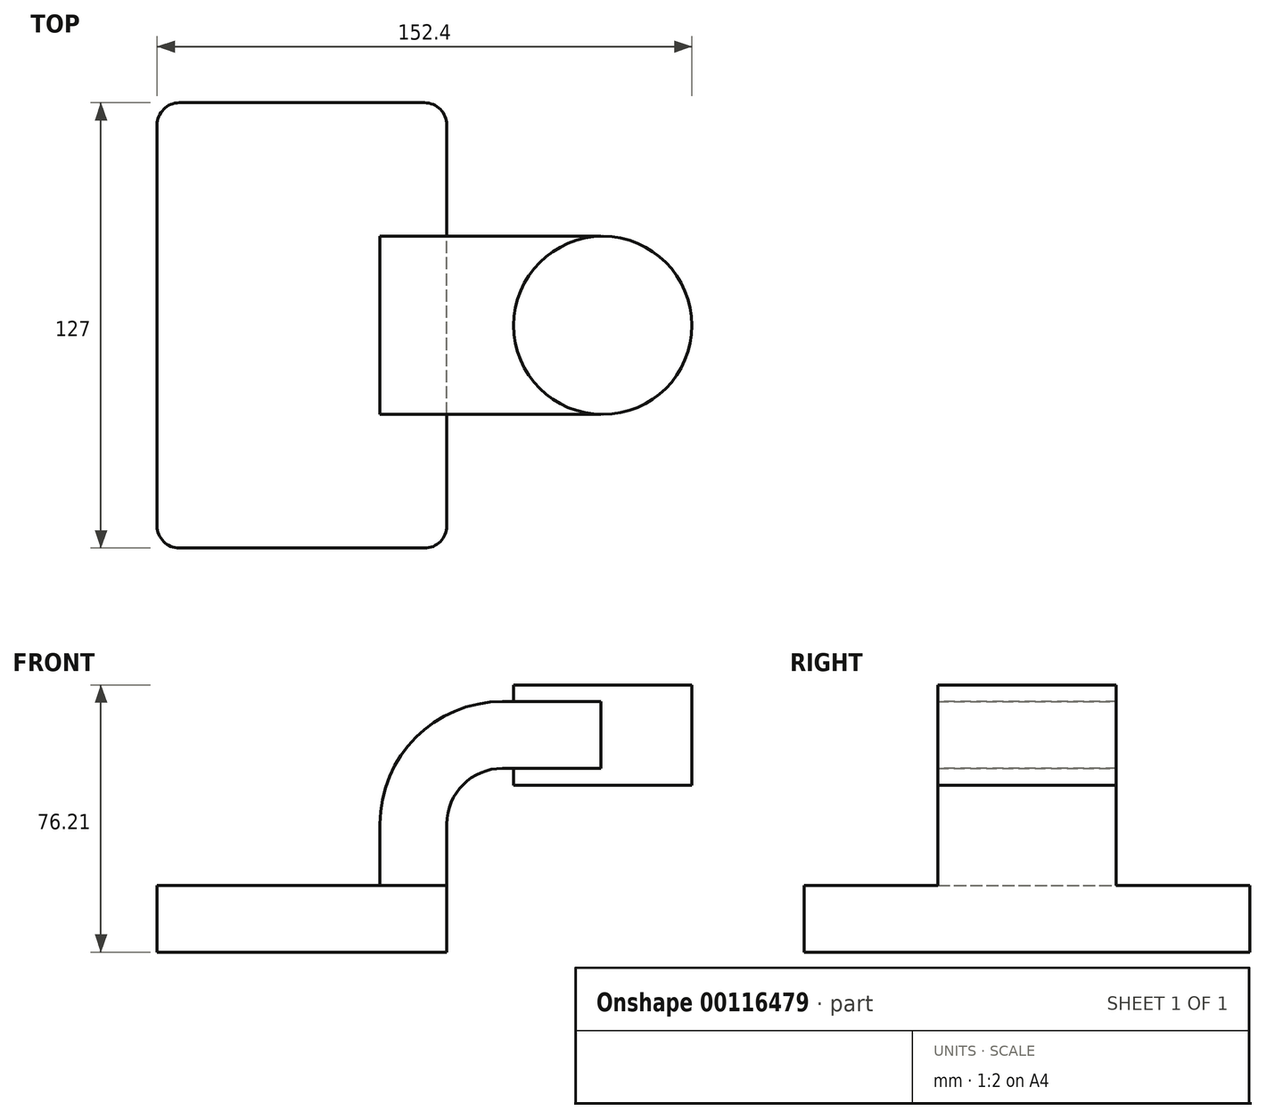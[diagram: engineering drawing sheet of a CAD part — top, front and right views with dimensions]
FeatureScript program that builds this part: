
annotation { "Feature Type Name" : "Feature", "Feature Type Description" : "" }
export const myFeature = defineFeature(function(context is Context, id is Id, definition is map)
    precondition{}
    {
        {
            var Q0;
            Q0=qCreatedBy(makeId("Front.planeOp"),FACE);
            var sketch = newSketch(context, id + "F0", { "sketchPlane" : qUnion([Q0])});
            skLineSegment(sketch, "E0.bottom", {"start": v(41.28, -9.52) * mm, "end": v(-41.28, -9.53) * mm});
            skLineSegment(sketch, "E0.top", {"start": v(41.27, 9.53) * mm, "end": v(-41.28, 9.53) * mm});
            skLineSegment(sketch, "E0.left", {"start": v(41.28, -9.52) * mm, "end": v(41.28, 9.53) * mm});
            skLineSegment(sketch, "E0.right", {"start": v(-41.28, -9.52) * mm, "end": v(-41.28, 9.53) * mm});
            skPoint(sketch, "E0.middle", {"position": v(0, 0) * mm});
            skLineSegment(sketch, "E1.bottom", {"start": v(60.32, 38.1) * mm, "end": v(111.12, 38.1) * mm});
            skLineSegment(sketch, "E1.top", {"start": v(60.32, 66.68) * mm, "end": v(111.12, 66.68) * mm});
            skLineSegment(sketch, "E1.left", {"start": v(60.32, 38.1) * mm, "end": v(60.32, 66.68) * mm});
            skLineSegment(sketch, "E1.right", {"start": v(111.12, 38.1) * mm, "end": v(111.12, 66.68) * mm});
            skPoint(sketch, "E1.middle", {"position": v(85.72, 52.39) * mm});
            skLineSegment(sketch, "E2", {"start": v(41.27, 9.53) * mm, "end": v(41.27, 27) * mm});
            skArc(sketch, "E3", {"start": v(41.27, 27) * mm, "mid": v(45.92, 38.23) * mm, "end": v(57.15, 42.88) * mm});
            skLineSegment(sketch, "E4", {"start": v(57.15, 42.88) * mm, "end": v(85.72, 42.88) * mm});
            skLineSegment(sketch, "E5.0", {"start": v(57.15, 61.93) * mm, "end": v(85.72, 61.93) * mm});
            skArc(sketch, "E5.1", {"start": v(22.23, 27) * mm, "mid": v(32.45, 51.7) * mm, "end": v(57.15, 61.93) * mm});
            skLineSegment(sketch, "E5.2", {"start": v(22.22, 9.53) * mm, "end": v(22.22, 27) * mm});
            skLineSegment(sketch, "E6", {"start": v(85.72, 66.68) * mm, "end": v(85.72, 38.1) * mm});
            skPoint(sketch, "E6.startSnap0", {"position": v(85.72, 66.68) * mm});
            skFitSpline(sketch, "E7", {"points": [v(-41.28, 9.53) * mm, v(57.15, 61.93) * mm], "startDerivative": vector(123.83, 60.16) * mm, "endDerivative": vector(171.45, -18.85) * mm});
            skSolve(sketch);
        }
        {
            var Q0;
            Q0=makeQuery(id+"F0.imprint","IMPRINT",FACE,{"disambiguationData":[TD([[makeQuery(id+"F0.imprint","IMPRINT",EDGE,{"derivedFrom":sQuery(id+"F0.wireOp",EDGE,"E0.bottom")}),-1.0]])]});
            extrude(context, id + "F1", {"entities" : qUnion([Q0]), "endBound" : BoundingType.SYMMETRIC, "depth" : 127 * mm});
        }
        {
            var Q0;
            {var subQ1=sQuery(id+"F0.wireOp",EDGE,"E2");Q0=makeQuery(id+"F0.imprint","IMPRINT",FACE,{"disambiguationData":[TD([[makeQuery(id+"F0.imprint","IMPRINT",EDGE,{"derivedFrom":subQ1}),1.0]])]});}
            var Q1;
            {var subQ0=sQuery(id+"F0.wireOp",EDGE,"E4");var subQ1=sQuery(id+"F0.wireOp",EDGE,"E1.left");var subQ2=makeQuery(id+"F0.imprint","INTERSECT",VERTEX,{"derivedFrom":[subQ1,subQ0]});Q1=makeQuery(id+"F0.imprint","IMPRINT",FACE,{"disambiguationData":[TD([[makeQuery(id+"F0.imprint","IMPRINT",EDGE,{"disambiguationData":[TD([[subQ2,-1.0]])],"derivedFrom":subQ1}),-1.0]])]});}
            extrude(context, id + "F2", {"entities" : qUnion([Q0, Q1]), "operationType" : NewBodyOperationType.ADD, "endBound" : BoundingType.SYMMETRIC, "depth" : 50.8 * mm});
        }
        {
            var Q0;
            Q0=makeQuery(id+"F0.imprint","IMPRINT",FACE,{"disambiguationData":[TD([[makeQuery(id+"F0.imprint","IMPRINT",EDGE,{"derivedFrom":sQuery(id+"F0.wireOp",EDGE,"E5.1")}),1.0]])]});
            extrude(context, id + "F3", {"entities" : qUnion([Q0]), "operationType" : NewBodyOperationType.ADD, "endBound" : BoundingType.SYMMETRIC, "depth" : 15.88 * mm});
        }
        {
            var Q0;
            {var subQ0=sQuery(id+"F0.wireOp",EDGE,"E1.right");Q0=makeQuery(id+"F0.imprint","IMPRINT",FACE,{"disambiguationData":[TD([[makeQuery(id+"F0.imprint","IMPRINT",EDGE,{"derivedFrom":subQ0}),1.0]])]});}
            var Q1;
            Q1=sQuery(id+"F0.wireOp",EDGE,"E6");
            revolve(context, id + "F4", {"operationType" : NewBodyOperationType.ADD, "entities" : qUnion([Q0]), "axis" : qUnion([Q1]), "revolveType" : RevolveType.FULL});
        }
        {
            var Q0;
            Q0=makeQuery(id+"F1.opExtrude","CAP_EDGE",EDGE,{"disambiguationData":[OSD([sQuery(id+"F0.wireOp",EDGE,"E0.right")])],"isStart":false});
            var Q1;
            Q1=makeQuery(id+"F1.opExtrude","CAP_EDGE",EDGE,{"disambiguationData":[OSD([sQuery(id+"F0.wireOp",EDGE,"E0.left")])],"isStart":false});
            var Q2;
            Q2=makeQuery(id+"F1.opExtrude","CAP_EDGE",EDGE,{"disambiguationData":[OSD([sQuery(id+"F0.wireOp",EDGE,"E0.left")])],"isStart":true});
            var Q3;
            Q3=makeQuery(id+"F1.opExtrude","CAP_EDGE",EDGE,{"disambiguationData":[OSD([sQuery(id+"F0.wireOp",EDGE,"E0.right")])],"isStart":true});
            fillet(context, id + "F5", {"entities" : qUnion([Q0, Q1, Q2, Q3]), "radius" : 6.35 * mm, "tangentPropagation" : true, "allowEdgeOverflow" : false});
        }
    });
